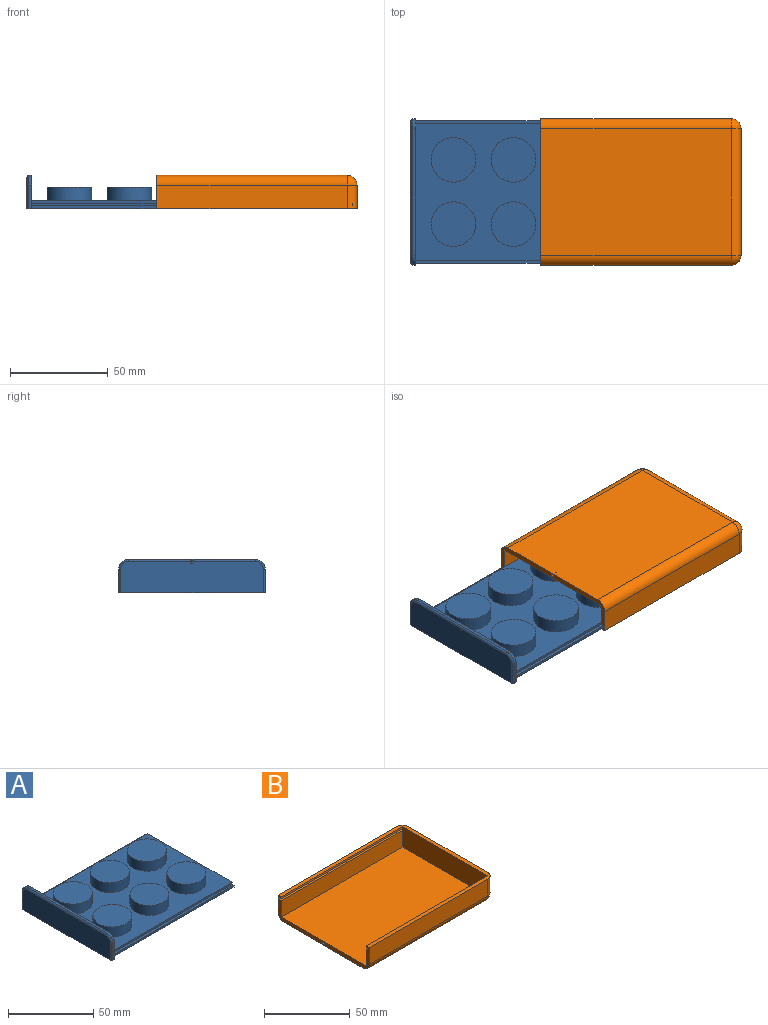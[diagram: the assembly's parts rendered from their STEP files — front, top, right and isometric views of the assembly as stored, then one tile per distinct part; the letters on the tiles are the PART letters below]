
ASSEMBLY  parts=2 mates=1
PART A: 64 faces, bbox 102.5x75.8x17.4 mm
  f0: plane 102.5x75mm, normal (0,0,-1), area 7087.1mm2, adj f3,f4,f5,f19,f20,f29,f30,f34
  f1: plane 100x1.35mm, normal (0,-1,0), area 135mm2, adj f5,f6,f20,f24
  f2: plane 100x1.35mm, normal (0,1,0), area 135mm2, adj f5,f6,f20,f21
  f3: plane 100x1.35mm, normal (0,1,0), area 135mm2, adj f0,f5,f20,f22
  f4: plane 100x1.35mm, normal (0,-1,0), area 135mm2, adj f0,f5,f20,f25
  f5: plane 73.2x4mm, normal (1,0,0), area 284.2mm2, adj f0,f1,f2,f3,f4,f6,f21,f22
  f6: plane 100x70mm, normal (0,0,1), area 4528.8mm2, adj f1,f2,f5,f7,f9,f11,f13,f15
  f7: cylinder r=11.45mm len=22.9mm, axis (0,0,-1), area 503.6mm2, adj f6,f8
  f8: plane 22.9x22.9mm, normal (0,0,1), area 411.9mm2, adj f7
  f9: cylinder r=11.45mm len=22.9mm, axis (0,0,-1), area 503.6mm2, adj f6,f10
  f10: plane 22.9x22.9mm, normal (0,0,1), area 411.9mm2, adj f9
  f11: cylinder r=11.45mm len=22.9mm, axis (0,0,-1), area 503.6mm2, adj f6,f12
  f12: plane 22.9x22.9mm, normal (0,0,1), area 411.9mm2, adj f11
  f13: cylinder r=11.45mm len=22.9mm, axis (0,0,-1), area 503.6mm2, adj f6,f14
  f14: plane 22.9x22.9mm, normal (0,0,1), area 411.9mm2, adj f13
  f15: cylinder r=11.45mm len=22.9mm, axis (0,0,-1), area 503.6mm2, adj f6,f16
  f16: plane 22.9x22.9mm, normal (0,0,1), area 411.9mm2, adj f15
  f17: cylinder r=11.45mm len=22.9mm, axis (0,0,-1), area 503.6mm2, adj f6,f18
  f18: plane 22.9x22.9mm, normal (0,0,1), area 411.9mm2, adj f17
  f19: plane 73x16mm, normal (-1,0,0), area 1161.1mm2, adj f0,f59,f60,f61,f62,f63
  f20: plane 75x17mm, normal (1,0,0), area 978mm2, adj f0,f1,f2,f3,f4,f6,f21,f22
  f21: plane 100x1.6mm, normal (0,0,1), area 160mm2, adj f2,f5,f20,f23
  f22: plane 100x1.6mm, normal (0,0,-1), area 160mm2, adj f3,f5,f20,f23
  f23: plane 100x1.3mm, normal (0,1,0), area 130mm2, adj f5,f20,f21,f22
  f24: plane 100x1.6mm, normal (0,0,1), area 160mm2, adj f1,f5,f20,f26
  f25: plane 100x1.6mm, normal (0,0,-1), area 160mm2, adj f4,f5,f20,f26
  f26: plane 100x1.3mm, normal (0,-1,0), area 130mm2, adj f5,f20,f24,f25
  f27: plane 65x1.5mm, normal (0,0,1), area 97.5mm2, adj f20,f28,f31,f61
  f28: cylinder r=5mm len=5mm, axis (1,0,0), area 11.8mm2, adj f20,f27,f29,f60
  f29: plane 12x1.5mm, normal (0,1,0), area 18mm2, adj f0,f20,f28,f59
  f30: plane 12x1.5mm, normal (0,-1,0), area 18mm2, adj f0,f20,f31,f63
  f31: cylinder r=5mm len=5mm, axis (1,0,0), area 11.8mm2, adj f20,f27,f30,f62
  f32: cylinder r=0.81mm len=2.2mm, axis (1,0,0), area 11.2mm2, adj f20,f33
  f33: plane 1.62x1.62mm, normal (1,0,0), area 2.1mm2, adj f32
  f34: plane 1x0.5mm, normal (0,1,0), area 0.5mm2, adj f0,f35,f37,f38
  f35: plane 20x0.5mm, normal (1,0,0), area 10mm2, adj f0,f34,f36,f38
  f36: plane 1x0.5mm, normal (0,-1,0), area 0.5mm2, adj f0,f35,f37,f38
  f37: plane 20x0.5mm, normal (-1,0,0), area 10mm2, adj f0,f34,f36,f38
  f38: plane 20x1mm, normal (0,0,-1), area 20mm2, adj f34,f35,f36,f37
  f39: plane 1x0.5mm, normal (0,1,0), area 0.5mm2, adj f0,f40,f42,f43
  f40: plane 20x0.5mm, normal (1,0,0), area 10mm2, adj f0,f39,f41,f43
  f41: plane 1x0.5mm, normal (0,-1,0), area 0.5mm2, adj f0,f40,f42,f43
  f42: plane 20x0.5mm, normal (-1,0,0), area 10mm2, adj f0,f39,f41,f43
  f43: plane 20x1mm, normal (0,0,-1), area 20mm2, adj f39,f40,f41,f42
  f44: plane 1x0.5mm, normal (0,1,0), area 0.5mm2, adj f0,f45,f47,f48
  f45: plane 20x0.5mm, normal (1,0,0), area 10mm2, adj f0,f44,f46,f48
  f46: plane 1x0.5mm, normal (0,-1,0), area 0.5mm2, adj f0,f45,f47,f48
  f47: plane 20x0.5mm, normal (-1,0,0), area 10mm2, adj f0,f44,f46,f48
  f48: plane 20x1mm, normal (0,0,-1), area 20mm2, adj f44,f45,f46,f47
  f49: plane 1x0.5mm, normal (0,1,0), area 0.5mm2, adj f0,f50,f52,f53
  f50: plane 20x0.5mm, normal (1,0,0), area 10mm2, adj f0,f49,f51,f53
  f51: plane 1x0.5mm, normal (0,-1,0), area 0.5mm2, adj f0,f50,f52,f53
  f52: plane 20x0.5mm, normal (-1,0,0), area 10mm2, adj f0,f49,f51,f53
  f53: plane 20x1mm, normal (0,0,-1), area 20mm2, adj f49,f50,f51,f52
  f54: plane 1x0.5mm, normal (0,1,0), area 0.5mm2, adj f0,f55,f57,f58
  f55: plane 20x0.5mm, normal (1,0,0), area 10mm2, adj f0,f54,f56,f58
  f56: plane 1x0.5mm, normal (0,-1,0), area 0.5mm2, adj f0,f55,f57,f58
  f57: plane 20x0.5mm, normal (-1,0,0), area 10mm2, adj f0,f54,f56,f58
  f58: plane 20x1mm, normal (0,0,-1), area 20mm2, adj f54,f55,f56,f57
  f59: cylinder r=1mm len=12mm, axis (0,0,1), area 18.8mm2, adj f0,f19,f29,f60
  f60: torus R=4mm, axis (-1,0,0), area 11.4mm2, adj f19,f28,f59,f61
  f61: cylinder r=1mm len=65mm, axis (0,-1,0), area 102.1mm2, adj f19,f27,f60,f62
  f62: torus R=4mm, axis (-1,0,0), area 11.4mm2, adj f19,f31,f61,f63
  f63: cylinder r=1mm len=12mm, axis (0,0,-1), area 18.8mm2, adj f0,f19,f30,f62
PART B: 27 faces, bbox 102.5x75x17 mm
  f0: plane 100x1.35mm, normal (0,-1,0), area 135mm2, adj f1,f3,f10,f15
  f1: plane 75x17mm, normal (-1,0,0), area 242.7mm2, adj f0,f2,f3,f4,f5,f7,f8,f9
  f2: plane 100x1.35mm, normal (0,1,0), area 135mm2, adj f1,f3,f10,f12
  f3: plane 102.5x75mm, normal (0,0,1), area 676.8mm2, adj f0,f1,f2,f4,f5,f6,f10,f18
  f4: plane 97.5x12mm, normal (0,1,0), area 1170mm2, adj f1,f3,f18,f19
  f5: plane 97.5x12mm, normal (0,-1,0), area 1170mm2, adj f1,f3,f22,f24
  f6: plane 65x12mm, normal (1,0,0), area 780mm2, adj f3,f18,f21,f24
  f7: plane 97.5x65mm, normal (0,0,-1), area 6337.5mm2, adj f1,f19,f21,f22
  f8: plane 100x11.75mm, normal (0,-1,0), area 1175mm2, adj f1,f10,f11,f17
  f9: plane 100x11.75mm, normal (0,1,0), area 1175mm2, adj f1,f10,f11,f13
  f10: plane 73.2x14.5mm, normal (-1,0,0), area 1019.5mm2, adj f0,f2,f3,f8,f9,f11,f12,f13
  f11: plane 100x70mm, normal (0,0,1), area 7000mm2, adj f1,f8,f9,f10
  f12: plane 100x1.6mm, normal (0,0,-1), area 160mm2, adj f1,f2,f10,f14
  f13: plane 100x1.6mm, normal (0,0,1), area 160mm2, adj f1,f9,f10,f14
  f14: plane 100x1.4mm, normal (0,1,0), area 140mm2, adj f1,f10,f12,f13
  f15: plane 100x1.6mm, normal (0,0,-1), area 160mm2, adj f0,f1,f10,f16
  f16: plane 100x1.4mm, normal (0,-1,0), area 140mm2, adj f1,f10,f15,f17
  f17: plane 100x1.6mm, normal (0,0,1), area 160mm2, adj f1,f8,f10,f16
  f18: cylinder r=5mm len=12mm, axis (0,0,-1), area 94.2mm2, adj f3,f4,f6,f20
  f19: cylinder r=5mm len=97.5mm, axis (-1,0,0), area 765.8mm2, adj f1,f4,f7,f20
  f20: sphere r=5mm, area 39.3mm2, adj f18,f19,f21
  f21: cylinder r=5mm len=65mm, axis (0,1,0), area 510.5mm2, adj f6,f7,f20,f23
  f22: cylinder r=5mm len=97.5mm, axis (1,0,0), area 765.8mm2, adj f1,f5,f7,f23
  f23: sphere r=5mm, area 39.3mm2, adj f21,f22,f24
  f24: cylinder r=5mm len=12mm, axis (0,0,1), area 94.2mm2, adj f3,f5,f6,f23
  f25: cylinder r=0.81mm len=2.2mm, axis (-1,0,0), area 11.2mm2, adj f1,f26
  f26: plane 1.62x1.62mm, normal (-1,0,0), area 2.1mm2, adj f25
PLACE A rot(axis=(0.44,0.36,-0.82),0deg) t=(-62.04,-40,-35.15)mm
PLACE B rot(axis=(-1,0,0),180deg) t=(3.26,-40,-20.15)mm
MATE slider B.f1 <-> A.f5  axis (-1,0,0) through (-47.99,-3.4,-35.8)mm
